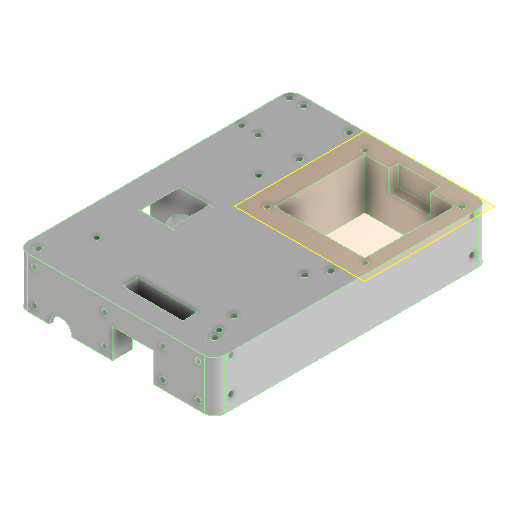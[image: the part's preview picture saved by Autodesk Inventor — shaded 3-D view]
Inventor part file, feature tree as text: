
AUTODESK INVENTOR PART (.ipt)
format: ipt  version: 2024.1 (Build 281209000, 209)  size: 494,592 bytes
history: native  units: mm
features: sketch x9, other x5, plane x2, hole x1, reference x1
ambient origin geometry x8: Origin, YZ Plane, XZ Plane, XY Plane, X Axis, Y Axis, Z Axis, Center Point
bodies: Volumenkörper1 (feature_tree)
feature tree (18):
  other  "60_Planktoscope_Base_half1.ipt"
  hole  "Bohrung1"  [1 undecoded]
  other  "Volumenkörper1::60_Planktoscope_Base_half1.ipt"
  other  "Bezeichnung1"
  sketch  "Skizze1"  dims[d0=10.0mm]
  sketch  "Skizze2"  dims[d1=2.8mm d2=6.0mm d3=4.0mm d4=2.0mm d5=90.0deg d6=12.0mm d7=20.594885mm]
  sketch  "Skizze3"
  sketch  "Skizze4"
  sketch  "Skizze5"
  sketch  "Skizze6"
  sketch  "Skizze8"
  sketch  "Skizze10"
  plane  "Arbeitsebene1"
  plane  "Arbeitsebene2"
  sketch  "Skizze12"
  reference  "Referenz5"
  other  "Assembly_Planktoscope_Uc2version_V1.iam"
  other  "00_UC2_ESP32-cnc_v3:1"
note: 1 required parameter value undecoded (feature->parameter linkage not recoverable at this tier; creation-order binding heuristic only, values carry confidence <= 0.55)
